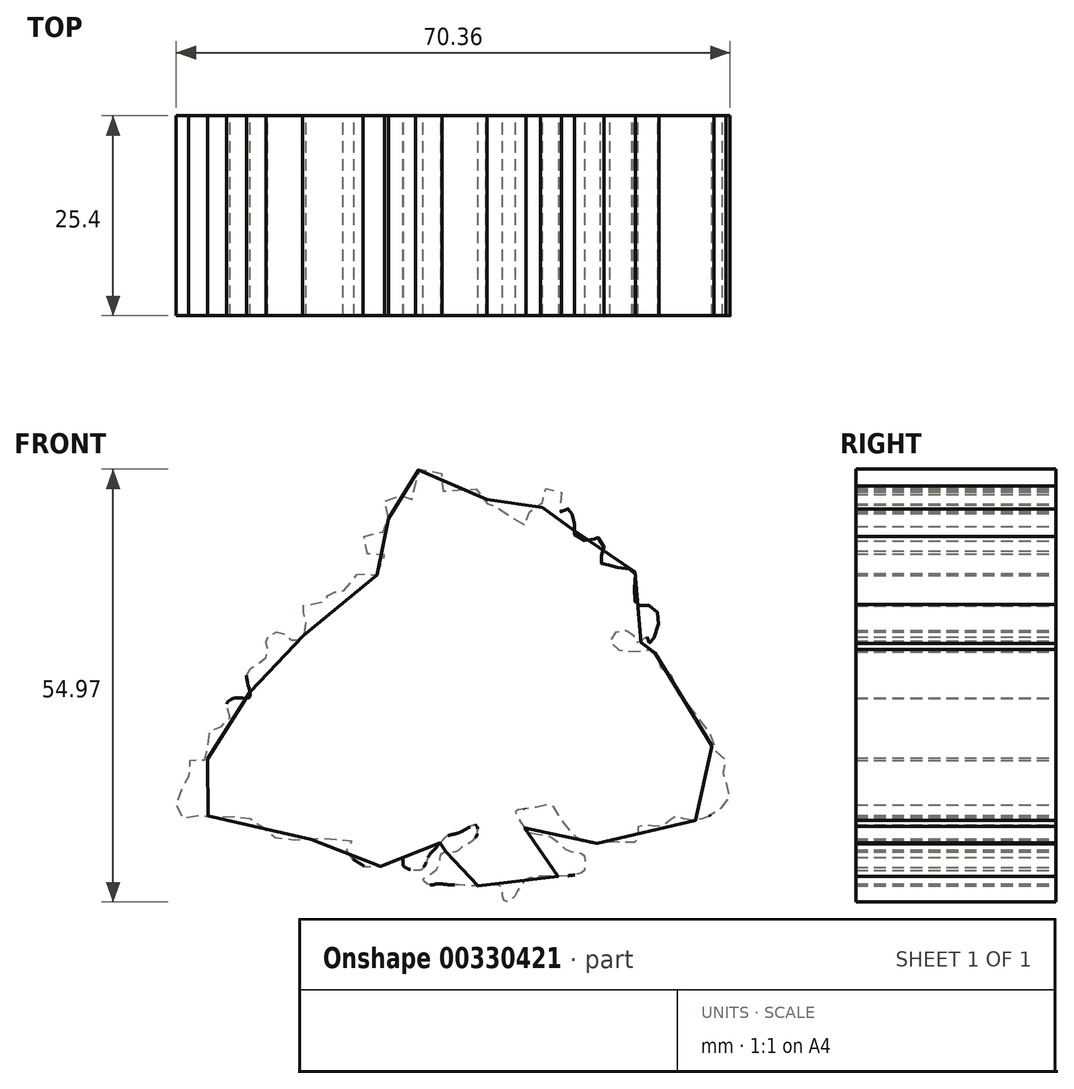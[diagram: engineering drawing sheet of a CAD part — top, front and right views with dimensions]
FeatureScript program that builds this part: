
annotation { "Feature Type Name" : "Feature", "Feature Type Description" : "" }
export const myFeature = defineFeature(function(context is Context, id is Id, definition is map)
    precondition{}
    {
        {
            var Q0;
            Q0=qCreatedBy(makeId("Front.planeOp"),FACE);
            var sketch = newSketch(context, id + "F0", { "sketchPlane" : qUnion([Q0])});
            skFitSpline(sketch, "E0", {"points": [v(14, 17.71) * mm, v(15.07, 19.31) * mm, v(14.53, 20.78) * mm, v(12.93, 20.38) * mm, v(12.26, 21.71) * mm, v(12.4, 22.65) * mm, v(14, 22.78) * mm, v(15.07, 23.58) * mm, v(15.33, 24.25) * mm, v(15.47, 25.32) * mm, v(15.2, 25.98) * mm, v(15.2, 27.72) * mm, v(16.8, 28.12) * mm, v(17.87, 26.78) * mm, v(18.4, 27.18) * mm, v(18.54, 27.72) * mm, v(18.94, 29.32) * mm, v(18.94, 30.52) * mm, v(19.2, 31.05) * mm, v(21.07, 31.05) * mm, v(22.27, 30.52) * mm, v(22.14, 29.72) * mm, v(22.8, 27.99) * mm, v(24.67, 28.52) * mm, v(25.47, 28.52) * mm, v(26.14, 28.39) * mm, v(27.2, 28.79) * mm, v(28, 26.78) * mm, v(27.88, 25.98) * mm, v(29.34, 26.52) * mm, v(30.41, 26.38) * mm, v(31.21, 24.38) * mm, v(32.68, 23.98) * mm, v(32.95, 25.05) * mm, v(33.08, 25.72) * mm, v(34.68, 25.58) * mm, v(34.95, 27.32) * mm, v(34.81, 28.12) * mm, v(35.88, 28.92) * mm, v(37.22, 28.79) * mm, v(37.35, 26.92) * mm, v(37.22, 25.72) * mm, v(38.28, 26.12) * mm, v(38.68, 25.72) * mm, v(39.08, 24.12) * mm, v(39.35, 22.51) * mm, v(41.62, 22.25) * mm, v(41.75, 22.65) * mm, v(42.82, 21.58) * mm, v(42.55, 20.25) * mm, v(42.55, 19.18) * mm, v(43.35, 19.05) * mm, v(44.82, 18.65) * mm, v(46.69, 18.24) * mm, v(46.69, 15.7) * mm, v(47.09, 13.84) * mm, v(48.02, 13.97) * mm, v(49.63, 13.04) * mm, v(49.5, 10.5) * mm, v(48.7, 9.04) * mm, v(48.42, 9.84) * mm, v(47.5, 9.17) * mm, v(46.42, 9.44) * mm, v(46.69, 10.24) * mm, v(45.62, 10.64) * mm, v(44.42, 10.5) * mm, v(43.62, 9.57) * mm, v(44.15, 8.5) * mm, v(46.56, 7.97) * mm, v(48.56, 8.24) * mm, v(49.76, 7.17) * mm, v(49.76, 6.24) * mm, v(50.96, 5.57) * mm, v(52.16, 2.9) * mm, v(54.56, 0) * mm, v(55.9, -2.04) * mm, v(56.83, -2.84) * mm, v(56.56, -4.3) * mm, v(57.76, -4.97) * mm, v(58.3, -6.57) * mm, v(57.9, -8.04) * mm, v(58.83, -9.64) * mm, v(58.3, -11.24) * mm, v(56.96, -12.44) * mm, v(55.36, -13.25) * mm, v(53.5, -13.38) * mm, v(51.76, -12.98) * mm, v(50.96, -13.78) * mm, v(49.1, -14.18) * mm, v(47.22, -14.18) * mm, v(47.09, -16.05) * mm, v(44.29, -16.18) * mm, v(40.42, -16.31) * mm, v(38.55, -14.71) * mm, v(37.22, -12.98) * mm, v(36.15, -11.51) * mm, v(33.75, -11.91) * mm, v(31.61, -12.31) * mm, v(32.55, -14.05) * mm, v(33.48, -14.98) * mm, v(35.61, -15.38) * mm, v(36.95, -16.18) * mm, v(38.55, -17.38) * mm, v(40.28, -17.78) * mm, v(40.42, -19.25) * mm, v(40.15, -20.05) * mm, v(35.61, -20.58) * mm, v(33.48, -20.72) * mm, v(32.28, -21.65) * mm, v(31.48, -23.12) * mm, v(30.54, -23.79) * mm, v(30.01, -23.25) * mm, v(29.88, -21.92) * mm, v(28.8, -21.65) * mm, v(26.4, -21.79) * mm, v(24.54, -21.65) * mm, v(23.34, -21.65) * mm, v(21.6, -21.52) * mm, v(20.8, -21.65) * mm, v(19.87, -20.98) * mm, v(21.34, -19.92) * mm, v(22, -18.45) * mm, v(22.4, -17.52) * mm, v(24, -17.38) * mm, v(24.94, -16.71) * mm, v(26.27, -15.91) * mm, v(26.8, -14.85) * mm, v(26.54, -14.05) * mm, v(25.07, -14.71) * mm, v(24.14, -15.11) * mm, v(22.8, -15.51) * mm, v(22.27, -16.05) * mm, v(21.74, -16.58) * mm, v(21.47, -16.98) * mm, v(20.8, -17.65) * mm, v(20.27, -18.72) * mm, v(19.74, -19.65) * mm, v(18.8, -19.78) * mm, v(17.33, -19.12) * mm, v(17.33, -18.18) * mm, v(16.4, -18.58) * mm, v(14.8, -19.25) * mm, v(12.93, -19.38) * mm, v(12.4, -19.25) * mm, v(9.73, -17.25) * mm, v(10.93, -17.11) * mm, v(10.66, -15.91) * mm, v(9.33, -15.91) * mm, v(7.06, -15.78) * mm, v(6.13, -15.91) * mm, v(4.8, -15.78) * mm, v(2.66, -16.05) * mm, v(0, -14.98) * mm, v(-1.21, -13.65) * mm, v(-2.28, -13.25) * mm, v(-4.15, -12.98) * mm, v(-5.88, -13.11) * mm, v(-8.42, -12.85) * mm, v(-10.55, -13.25) * mm, v(-11.49, -11.78) * mm, v(-10.55, -8.98) * mm, v(-9.89, -8.3) * mm, v(-9.89, -6.84) * mm, v(-9.35, -5.5) * mm, v(-7.62, -5.77) * mm, v(-7.48, -4.04) * mm, v(-7.22, -2.17) * mm, v(-6.28, -1.64) * mm, v(-4.95, -1.1) * mm, v(-4.68, 0) * mm, v(-5.08, 1.3) * mm, v(-3.88, 2.1) * mm, v(-2.15, 2.23) * mm, v(-2.55, 4.77) * mm, v(-1.75, 6.1) * mm, v(0, 7.44) * mm, v(0, 9.04) * mm, v(0, 9.7) * mm, v(1.72, 10.5) * mm, v(3.2, 9.44) * mm, v(4.53, 9.84) * mm, v(4.93, 12.1) * mm, v(4.66, 13.84) * mm, v(7.06, 14.24) * mm, v(8.13, 15.44) * mm, v(10, 15.84) * mm, v(11.6, 17.84) * mm, v(14, 17.71) * mm]});
            skCircle(sketch, "E1", {"center": v(21.31, -4.29) * mm, "radius": 68.33 * mm});
            skPoint(sketch, "E1.first.point", {"position": v(-10.94, 55.95) * mm});
            skPoint(sketch, "E1.second.point", {"position": v(51.76, -65.46) * mm});
            skPoint(sketch, "E1.third.point", {"position": v(65.71, -56.23) * mm});
            skSolve(sketch);
        }
        {
            var Q0;
            Q0=makeQuery(id+"F0.imprint","IMPRINT",FACE,{"disambiguationData":[TD([[makeQuery(id+"F0.imprint","IMPRINT",EDGE,{"derivedFrom":sQuery(id+"F0.wireOp",EDGE,"E0")}),-1.0]])]});
            extrude(context, id + "F1", {"entities" : qUnion([Q0]), "depth" : 25.4 * mm});
        }
    });
